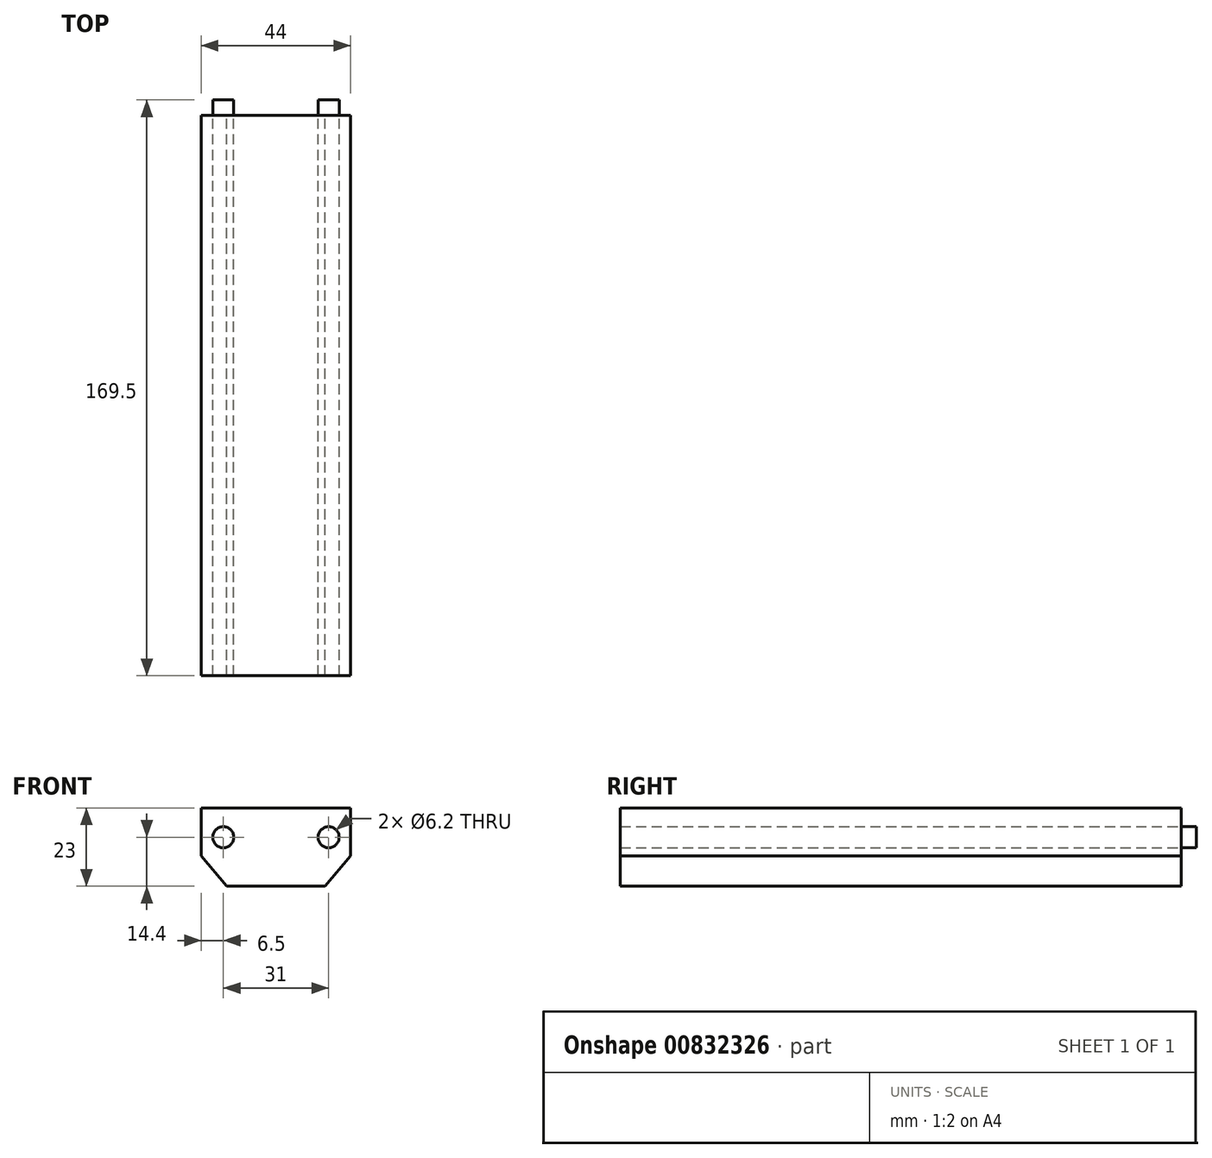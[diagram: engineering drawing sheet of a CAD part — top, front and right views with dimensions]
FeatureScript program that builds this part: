
annotation { "Feature Type Name" : "Feature", "Feature Type Description" : "" }
export const myFeature = defineFeature(function(context is Context, id is Id, definition is map)
    precondition{}
    {
        {
            var Q0;
            Q0=qCreatedBy(makeId("Front.planeOp"),FACE);
            var sketch = newSketch(context, id + "F0", { "sketchPlane" : qUnion([Q0])});
            skPoint(sketch, "E0", {"position": v(0, 14.1) * mm});
            skLineSegment(sketch, "E1", {"start": v(0, 14.1) * mm, "end": v(0, 0) * mm, "construction": true});
            skLineSegment(sketch, "E2", {"start": v(-14.5, -8.9) * mm, "end": v(14.5, -8.9) * mm});
            skPoint(sketch, "E3", {"position": v(0, -8.9) * mm});
            skLineSegment(sketch, "E4", {"start": v(0, 0) * mm, "end": v(0, -8.9) * mm, "construction": true});
            skLineSegment(sketch, "E5", {"start": v(14.5, -8.9) * mm, "end": v(22, 0) * mm});
            skLineSegment(sketch, "E6", {"start": v(-14.5, -8.9) * mm, "end": v(-22, 0) * mm});
            skArc(sketch, "E7", {"start": v(22, 0) * mm, "mid": v(16.61, -3.07) * mm, "end": v(14.5, -8.9) * mm});
            skArc(sketch, "E8", {"start": v(-14.5, -8.9) * mm, "mid": v(-16.61, -3.07) * mm, "end": v(-22, 0) * mm});
            skLineSegment(sketch, "E9", {"start": v(-15.5, 5.5) * mm, "end": v(15.5, 5.5) * mm, "construction": true});
            skCircle(sketch, "E10", {"center": v(-15.5, 5.5) * mm, "radius": 3.1 * mm});
            skCircle(sketch, "E11", {"center": v(15.5, 5.5) * mm, "radius": 3.1 * mm});
            skPoint(sketch, "E12", {"position": v(0, 5.5) * mm});
            skLineSegment(sketch, "E13.bottom", {"start": v(-22, 0) * mm, "end": v(22, 0) * mm});
            skLineSegment(sketch, "E13.top", {"start": v(-22, 14.1) * mm, "end": v(22, 14.1) * mm});
            skLineSegment(sketch, "E13.left", {"start": v(-22, 0) * mm, "end": v(-22, 14.1) * mm});
            skLineSegment(sketch, "E13.right", {"start": v(22, 0) * mm, "end": v(22, 14.1) * mm});
            skSolve(sketch);
        }
        {
            var Q0;
            Q0=makeQuery(id+"F0.imprint","IMPRINT",FACE,{"disambiguationData":[TD([[makeQuery(id+"F0.imprint","IMPRINT",EDGE,{"derivedFrom":sQuery(id+"F0.wireOp",EDGE,"E10")}),-1.0]])]});
            var Q1;
            Q1=makeQuery(id+"F0.imprint","IMPRINT",FACE,{"disambiguationData":[TD([[makeQuery(id+"F0.imprint","IMPRINT",EDGE,{"derivedFrom":sQuery(id+"F0.wireOp",EDGE,"E2")}),1.0]])]});
            var Q2;
            Q2=makeQuery(id+"F0.imprint","IMPRINT",FACE,{"disambiguationData":[TD([[makeQuery(id+"F0.imprint","IMPRINT",EDGE,{"derivedFrom":sQuery(id+"F0.wireOp",EDGE,"E6")}),-1.0]])]});
            var Q3;
            Q3=makeQuery(id+"F0.imprint","IMPRINT",FACE,{"disambiguationData":[TD([[makeQuery(id+"F0.imprint","IMPRINT",EDGE,{"derivedFrom":sQuery(id+"F0.wireOp",EDGE,"E5")}),1.0]])]});
            extrude(context, id + "F1", {"entities" : qUnion([Q0, Q1, Q2, Q3]), "depth" : 165 * mm, "offsetDistance" : 25 * mm});
        }
        {
            var Q0;
            Q0=makeQuery(id+"F0.imprint","IMPRINT",FACE,{"disambiguationData":[TD([[makeQuery(id+"F0.imprint","IMPRINT",EDGE,{"derivedFrom":sQuery(id+"F0.wireOp",EDGE,"E10")}),1.0]])]});
            var Q1;
            Q1=makeQuery(id+"F0.imprint","IMPRINT",FACE,{"disambiguationData":[TD([[makeQuery(id+"F0.imprint","IMPRINT",EDGE,{"derivedFrom":sQuery(id+"F0.wireOp",EDGE,"E11")}),1.0]])]});
            extrude(context, id + "F2", {"entities" : qUnion([Q0, Q1]), "operationType" : NewBodyOperationType.ADD, "oppositeDirection" : true, "depth" : 4.5 * mm, "offsetDistance" : 25 * mm});
        }
    });
